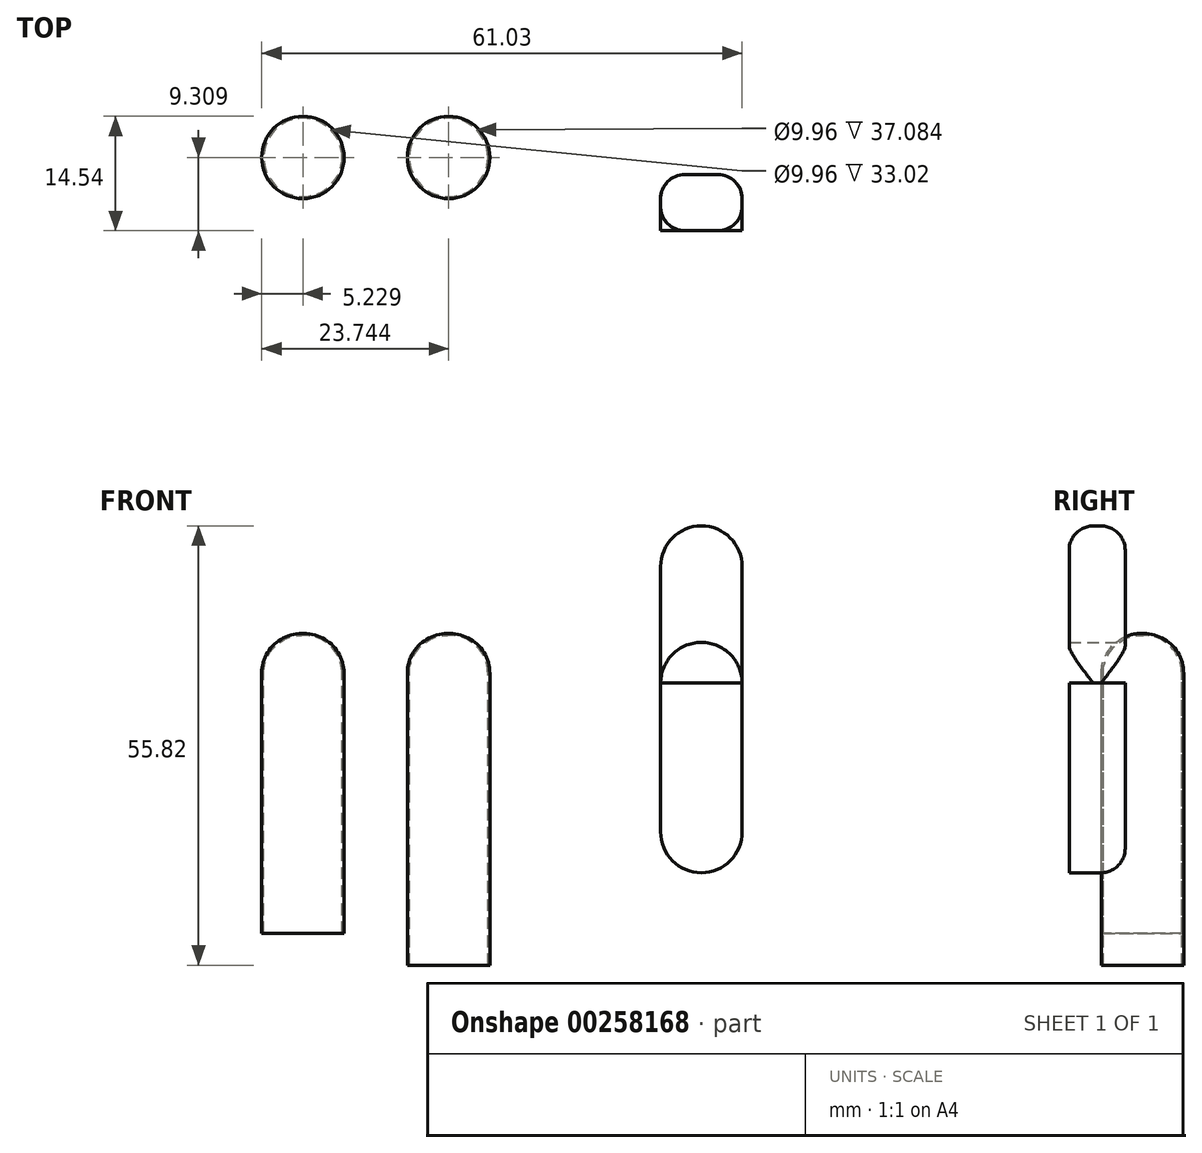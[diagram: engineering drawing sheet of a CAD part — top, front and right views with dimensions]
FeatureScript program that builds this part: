
annotation { "Feature Type Name" : "Feature", "Feature Type Description" : "" }
export const myFeature = defineFeature(function(context is Context, id is Id, definition is map)
    precondition{}
    {
        {
            var Q0;
            Q0=qCreatedBy(makeId("Front.planeOp"),FACE);
            var sketch = newSketch(context, id + "F0", { "sketchPlane" : qUnion([Q0])});
            skLineSegment(sketch, "E0", {"start": v(-5.46, -25.22) * mm, "end": v(-5.46, -6.32) * mm});
            skLineSegment(sketch, "E1", {"start": v(4.9, -25.22) * mm, "end": v(4.9, -6.32) * mm});
            skLineSegment(sketch, "E2", {"start": v(4.9, -6.32) * mm, "end": v(4.9, 0.66) * mm});
            skArc(sketch, "E3", {"start": v(-5.46, -6.32) * mm, "mid": v(-0.28, -1.14) * mm, "end": v(4.9, -6.32) * mm});
            skArc(sketch, "E4", {"start": v(-5.46, -6.32) * mm, "mid": v(-0.28, -11.5) * mm, "end": v(4.9, -6.32) * mm});
            skLineSegment(sketch, "E5", {"start": v(-5.46, -6.32) * mm, "end": v(4.9, -6.32) * mm});
            skLineSegment(sketch, "E6", {"start": v(-5.46, -6.32) * mm, "end": v(-5.46, 8.48) * mm});
            skLineSegment(sketch, "E7", {"start": v(4.9, 0.66) * mm, "end": v(4.9, 8.48) * mm});
            skArc(sketch, "E8", {"start": v(-5.46, 8.48) * mm, "mid": v(-0.28, 13.66) * mm, "end": v(4.9, 8.48) * mm});
            skArc(sketch, "E9", {"start": v(-5.46, -25.22) * mm, "mid": v(-0.28, -30.4) * mm, "end": v(4.9, -25.22) * mm});
            skSolve(sketch);
        }
        {
            var Q0;
            Q0=makeQuery(id+"F0.imprint","IMPRINT",FACE,{"disambiguationData":[TD([[makeQuery(id+"F0.imprint","IMPRINT",EDGE,{"derivedFrom":sQuery(id+"F0.wireOp",EDGE,"E2")}),1.0]])]});
            var Q1;
            Q1=makeQuery(id+"F0.imprint","IMPRINT",FACE,{"disambiguationData":[TD([[makeQuery(id+"F0.imprint","IMPRINT",EDGE,{"derivedFrom":sQuery(id+"F0.wireOp",EDGE,"E3")}),-1.0]])]});
            var Q2;
            Q2=makeQuery(id+"F0.imprint","IMPRINT",FACE,{"disambiguationData":[TD([[makeQuery(id+"F0.imprint","IMPRINT",EDGE,{"derivedFrom":sQuery(id+"F0.wireOp",EDGE,"E4")}),1.0]])]});
            var Q3;
            Q3=makeQuery(id+"F0.imprint","IMPRINT",FACE,{"disambiguationData":[TD([[makeQuery(id+"F0.imprint","IMPRINT",EDGE,{"derivedFrom":sQuery(id+"F0.wireOp",EDGE,"E0")}),-1.0]])]});
            extrude(context, id + "F1", {"entities" : qUnion([Q0, Q1, Q2, Q3]), "depth" : 7.11 * mm});
        }
        {
            var Q0;
            Q0=makeQuery(id+"F1.opExtrude","CAP_EDGE",EDGE,{"disambiguationData":[OSD([sQuery(id+"F0.wireOp",EDGE,"E1"),sQuery(id+"F0.wireOp",EDGE,"E2"),sQuery(id+"F0.wireOp",EDGE,"E7")])],"isStart":false});
            var Q1;
            Q1=makeQuery(id+"F1.opExtrude","CAP_EDGE",EDGE,{"disambiguationData":[OSD([sQuery(id+"F0.wireOp",EDGE,"E1"),sQuery(id+"F0.wireOp",EDGE,"E2"),sQuery(id+"F0.wireOp",EDGE,"E7")])],"isStart":true});
            var Q2;
            Q2=makeQuery(id+"F1.opExtrude","CAP_EDGE",EDGE,{"disambiguationData":[OSD([sQuery(id+"F0.wireOp",EDGE,"E0"),sQuery(id+"F0.wireOp",EDGE,"E6")])],"isStart":true});
            fillet(context, id + "F2", {"entities" : qUnion([Q0, Q1, Q2]), "radius" : 3.07 * mm, "tangentPropagation" : true, "allowEdgeOverflow" : false});
        }
        {
            var Q0;
            Q0=qCreatedBy(makeId("Top.planeOp"),FACE);
            var sketch = newSketch(context, id + "F3", { "sketchPlane" : qUnion([Q0])});
            skCircle(sketch, "E10", {"center": v(-32.39, 2.2) * mm, "radius": 5.23 * mm});
            skCircle(sketch, "E11", {"center": v(-50.9, 2.2) * mm, "radius": 5.23 * mm});
            skSolve(sketch);
        }
        {
            var Q0;
            Q0=makeQuery(id+"F3.imprint","IMPRINT",FACE,{"disambiguationData":[TD([[makeQuery(id+"F3.imprint","IMPRINT",EDGE,{"derivedFrom":sQuery(id+"F3.wireOp",EDGE,"E10")}),1.0]])]});
            extrude(context, id + "F4", {"entities" : qUnion([Q0]), "oppositeDirection" : true, "depth" : 42.16 * mm});
        }
        {
            var Q0;
            Q0=makeQuery(id+"F4.opExtrude","CAP_EDGE",EDGE,{"disambiguationData":[OSD([sQuery(id+"F3.wireOp",EDGE,"E10")])],"isStart":true});
            fillet(context, id + "F5", {"entities" : qUnion([Q0]), "radius" : 5.08 * mm, "tangentPropagation" : true, "allowEdgeOverflow" : false});
        }
        {
            var Q0;
            Q0=makeQuery(id+"F4.opExtrude","CAP_FACE",FACE,{"disambiguationData":[OSD([sQuery(id+"F3.wireOp",EDGE,"E10")])],"isStart":false});
            shell(context, id + "F6", {"entities" : qUnion([Q0]), "thickness" : 0.25 * mm});
        }
        {
            var Q0;
            Q0=makeQuery(id+"F3.imprint","IMPRINT",FACE,{"disambiguationData":[TD([[makeQuery(id+"F3.imprint","IMPRINT",EDGE,{"derivedFrom":sQuery(id+"F3.wireOp",EDGE,"E11")}),1.0]])]});
            extrude(context, id + "F7", {"entities" : qUnion([Q0]), "oppositeDirection" : true, "depth" : 38.1 * mm});
        }
        {
            var Q0;
            Q0=makeQuery(id+"F7.opExtrude","CAP_EDGE",EDGE,{"disambiguationData":[OSD([sQuery(id+"F3.wireOp",EDGE,"E11")])],"isStart":true});
            fillet(context, id + "F8", {"entities" : qUnion([Q0]), "radius" : 5.08 * mm, "tangentPropagation" : true, "allowEdgeOverflow" : false});
        }
        {
            var Q0;
            Q0=makeQuery(id+"F7.opExtrude","CAP_FACE",FACE,{"disambiguationData":[OSD([sQuery(id+"F3.wireOp",EDGE,"E11")])],"isStart":false});
            shell(context, id + "F9", {"entities" : qUnion([Q0]), "thickness" : 0.25 * mm});
        }
    });
